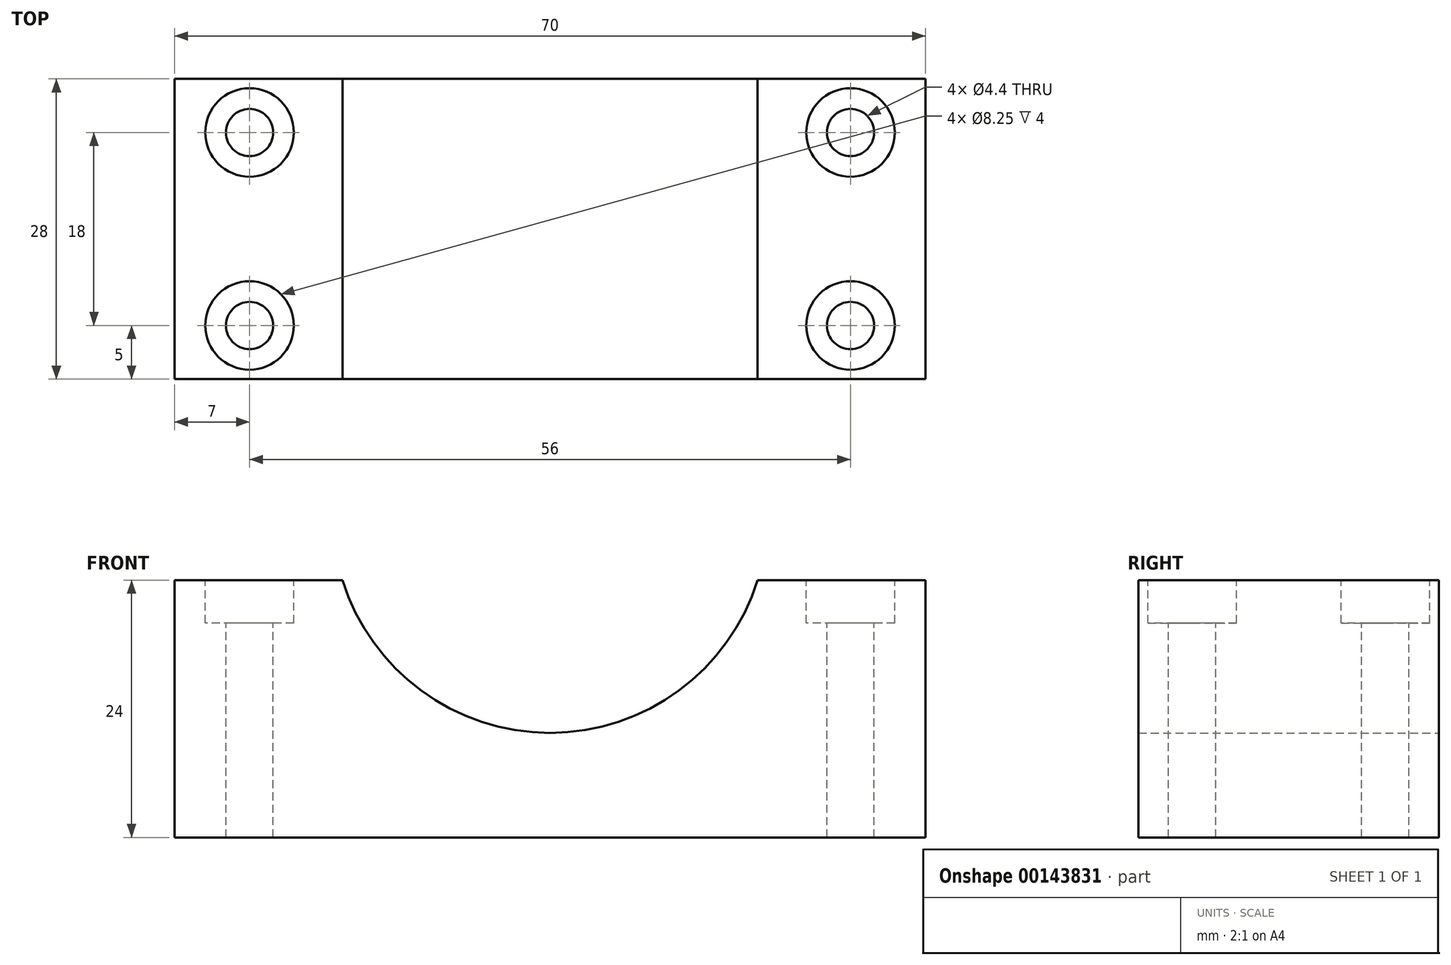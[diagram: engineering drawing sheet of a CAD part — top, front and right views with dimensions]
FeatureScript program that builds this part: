
annotation { "Feature Type Name" : "Feature", "Feature Type Description" : "" }
export const myFeature = defineFeature(function(context is Context, id is Id, definition is map)
    precondition{}
    {
        {
            var Q0;
            Q0=qCreatedBy(makeId("Front.planeOp"),FACE);
            var sketch = newSketch(context, id + "F0", { "sketchPlane" : qUnion([Q0])});
            skLineSegment(sketch, "E0.bottom", {"start": v(35, -15) * mm, "end": v(-35, -15) * mm});
            skLineSegment(sketch, "E0.left", {"start": v(35, -15) * mm, "end": v(35, 9) * mm});
            skLineSegment(sketch, "E0.right", {"start": v(-35, -15) * mm, "end": v(-35, 9) * mm});
            skPoint(sketch, "E0.middle", {"position": v(0, 0) * mm});
            skArc(sketch, "E1", {"start": v(-19.34, 9) * mm, "mid": v(0, -5.25) * mm, "end": v(19.34, 9) * mm});
            skLineSegment(sketch, "E2", {"start": v(35, 9) * mm, "end": v(19.34, 9) * mm});
            skLineSegment(sketch, "E3.trimOffspring", {"start": v(-19.34, 9) * mm, "end": v(-35, 9) * mm});
            skSolve(sketch);
        }
        {
            var Q0;
            Q0=makeQuery(id+"F0.imprint","IMPRINT",FACE,{"disambiguationData":[TD([[makeQuery(id+"F0.imprint","IMPRINT",EDGE,{"derivedFrom":sQuery(id+"F0.wireOp",EDGE,"E0.bottom")}),-1.0]])]});
            extrude(context, id + "F1", {"entities" : qUnion([Q0]), "depth" : 28 * mm});
        }
        {
            var Q0;
            Q0=makeQuery(id+"F1.opExtrude","SWEPT_FACE",FACE,{"disambiguationData":[OSD([sQuery(id+"F0.wireOp",EDGE,"E3.trimOffspring")])]});
            var sketch = newSketch(context, id + "F2", { "sketchPlane" : qUnion([Q0])});
            skCircle(sketch, "E4", {"center": v(-28, -5) * mm, "radius": 1.65 * mm});
            skCircle(sketch, "E5", {"center": v(-28, -23) * mm, "radius": 1.7 * mm});
            skCircle(sketch, "E6", {"center": v(28, -5) * mm, "radius": 1.6 * mm});
            skCircle(sketch, "E7", {"center": v(28, -23) * mm, "radius": 1.65 * mm});
            skSolve(sketch);
        }
        {
            var Q0;
            Q0=sQuery(id+"F2.wireOp",VERTEX,"E4.center");
            var Q1;
            Q1=sQuery(id+"F2.wireOp",VERTEX,"E5.center");
            var Q2;
            Q2=sQuery(id+"F2.wireOp",VERTEX,"E7.center");
            var Q3;
            Q3=sQuery(id+"F2.wireOp",VERTEX,"E6.center");
            var Q4;
            Q4=makeQuery(id+"F1.opExtrude","SWEPT_BODY",BODY,{"disambiguationData":[OSD([sQuery(id+"F0.wireOp",EDGE,"E0.bottom"),sQuery(id+"F0.wireOp",EDGE,"E0.left"),sQuery(id+"F0.wireOp",EDGE,"E0.right"),sQuery(id+"F0.wireOp",EDGE,"E1"),sQuery(id+"F0.wireOp",EDGE,"E2"),sQuery(id+"F0.wireOp",EDGE,"E3.trimOffspring")])]});
            hole(context, id + "F3", {"style" : HoleStyle.C_BORE, "endStyle" : HoleEndStyle.THROUGH, "standardTappedOrClearance" : lookupTablePath({ "standard" : "ISO", "fit" : "Normal", "size" : "M4", "type" : "Clearance" }), "standardBlindInLast" : lookupTablePath({ "fit" : "Standard", "standard" : "ISO", "size" : "M4", "type" : "Clearance" }), "holeDiameter" : 4.4 * mm, "cBoreDiameter" : 8.25 * mm, "cBoreDepth" : 4 * mm, "startFromSketch" : true, "locations" : qUnion([Q0, Q1, Q2, Q3]), "scope" : qUnion([Q4]), "isTappedThrough" : true});
        }
    });
